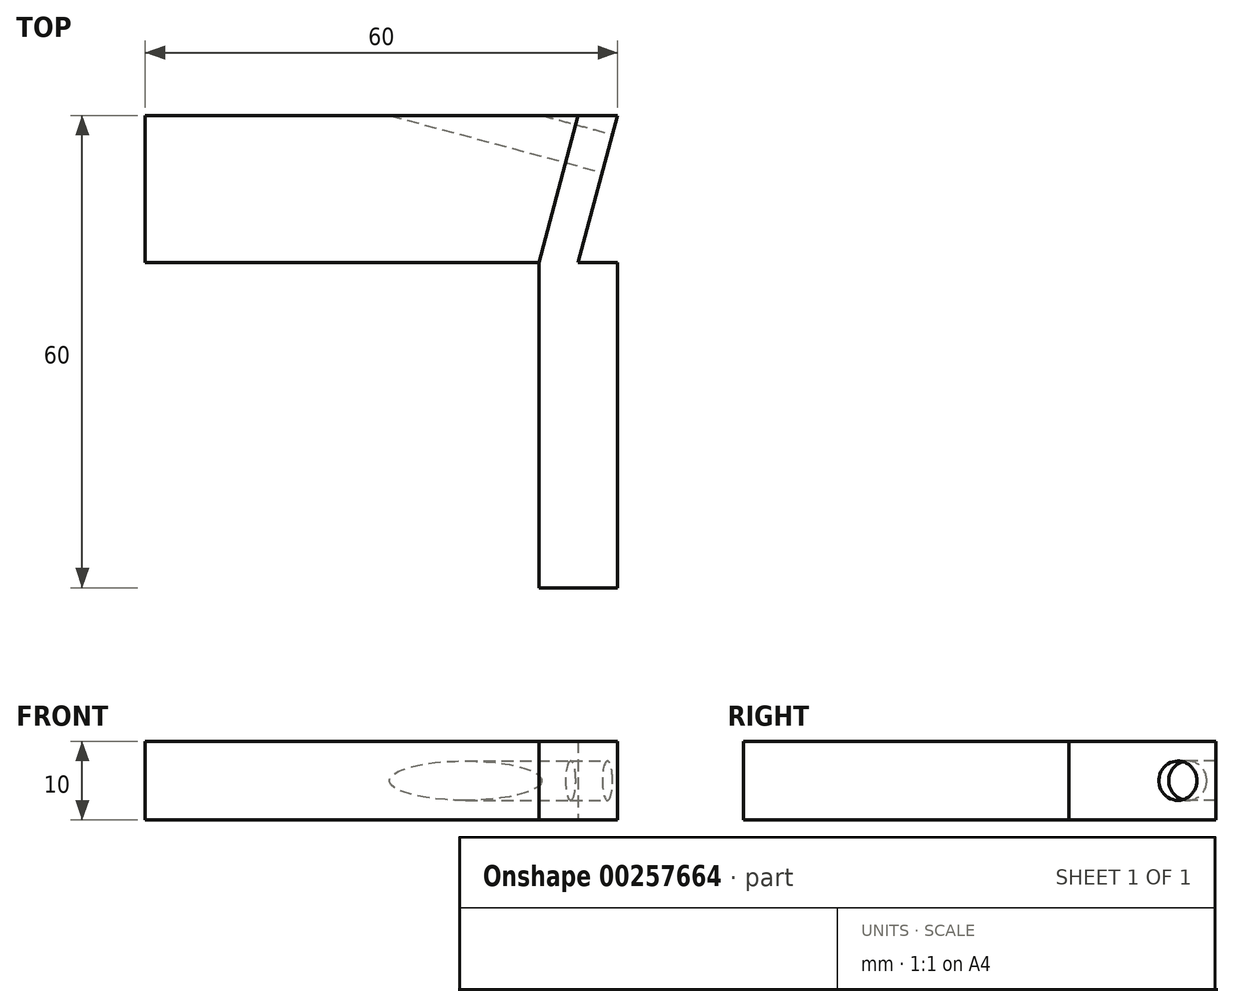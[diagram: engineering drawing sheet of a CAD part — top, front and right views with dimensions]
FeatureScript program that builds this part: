
annotation { "Feature Type Name" : "Feature", "Feature Type Description" : "" }
export const myFeature = defineFeature(function(context is Context, id is Id, definition is map)
    precondition{}
    {
        {
            var Q0;
            Q0=qCreatedBy(makeId("Top.planeOp"),FACE);
            var sketch = newSketch(context, id + "F0", { "sketchPlane" : qUnion([Q0])});
            skLineSegment(sketch, "E0.bottom", {"start": v(0, 0) * mm, "end": v(10, 0) * mm});
            skLineSegment(sketch, "E0.top", {"start": v(0, -60) * mm, "end": v(10, -60) * mm});
            skLineSegment(sketch, "E0.left", {"start": v(0, 0) * mm, "end": v(0, -60) * mm});
            skLineSegment(sketch, "E0.right", {"start": v(10, 0) * mm, "end": v(10, -60) * mm});
            skLineSegment(sketch, "E1", {"start": v(5, 0) * mm, "end": v(0, -18.66) * mm});
            skLineSegment(sketch, "E2", {"start": v(0, -18.66) * mm, "end": v(-50, -18.66) * mm});
            skLineSegment(sketch, "E3", {"start": v(-50, -18.66) * mm, "end": v(-50, 0) * mm});
            skLineSegment(sketch, "E4", {"start": v(-50, 0) * mm, "end": v(5, 0) * mm});
            skLineSegment(sketch, "E5", {"start": v(10, 0) * mm, "end": v(5, -18.66) * mm});
            skLineSegment(sketch, "E6", {"start": v(5, -18.66) * mm, "end": v(10, -18.66) * mm});
            skSolve(sketch);
        }
        {
            var Q0;
            {var subQ2=sQuery(id+"F0.wireOp",EDGE,"E0.top");Q0=makeQuery(id+"F0.imprint","IMPRINT",FACE,{"disambiguationData":[TD([[makeQuery(id+"F0.imprint","IMPRINT",EDGE,{"derivedFrom":subQ2}),1.0]])]});}
            extrude(context, id + "F1", {"entities" : qUnion([Q0]), "depth" : 10 * mm});
        }
        {
            var Q0;
            {var subQ3=sQuery(id+"F0.wireOp",EDGE,"E2");Q0=makeQuery(id+"F0.imprint","IMPRINT",FACE,{"disambiguationData":[TD([[makeQuery(id+"F0.imprint","IMPRINT",EDGE,{"derivedFrom":subQ3}),-1.0]])]});}
            var Q1;
            {var subQ3=sQuery(id+"F0.wireOp",EDGE,"E1");Q1=makeQuery(id+"F0.imprint","IMPRINT",FACE,{"disambiguationData":[TD([[makeQuery(id+"F0.imprint","IMPRINT",EDGE,{"derivedFrom":subQ3}),-1.0]])]});}
            extrude(context, id + "F2", {"entities" : qUnion([Q0, Q1]), "depth" : 10 * mm});
        }
        {
            var Q0;
            Q0=makeQuery(id+"F1.opExtrude","SWEPT_FACE",FACE,{"disambiguationData":[OSD([sQuery(id+"F0.wireOp",EDGE,"E5")])]});
            var sketch = newSketch(context, id + "F3", { "sketchPlane" : qUnion([Q0])});
            skPoint(sketch, "E7", {"position": v(-2.41, 5) * mm});
            skSolve(sketch);
        }
        {
            var Q0;
            Q0=sQuery(id+"F3.wireOp",VERTEX,"E7");
            var Q1;
            Q1=makeQuery(id+"F1.opExtrude","SWEPT_BODY",BODY,{"disambiguationData":[OSD([sQuery(id+"F0.wireOp",EDGE,"E0.bottom"),sQuery(id+"F0.wireOp",EDGE,"E0.top"),sQuery(id+"F0.wireOp",EDGE,"E0.left"),sQuery(id+"F0.wireOp",EDGE,"E0.right"),sQuery(id+"F0.wireOp",EDGE,"E1"),sQuery(id+"F0.wireOp",EDGE,"E5"),sQuery(id+"F0.wireOp",EDGE,"E6")])]});
            var Q2;
            Q2=makeQuery(id+"F2.opExtrude","SWEPT_BODY",BODY,{"disambiguationData":[OSD([sQuery(id+"F0.wireOp",EDGE,"E1"),sQuery(id+"F0.wireOp",EDGE,"E2"),sQuery(id+"F0.wireOp",EDGE,"E3"),sQuery(id+"F0.wireOp",EDGE,"E4")])]});
            hole(context, id + "F4", {"style" : HoleStyle.SIMPLE, "endStyle" : HoleEndStyle.THROUGH, "holeDiameter" : 5 * mm, "tappedDepth" : 7 * mm, "tapClearance" : 3, "startFromSketch" : true, "locations" : qUnion([Q0]), "scope" : qUnion([Q1, Q2])});
        }
    });
